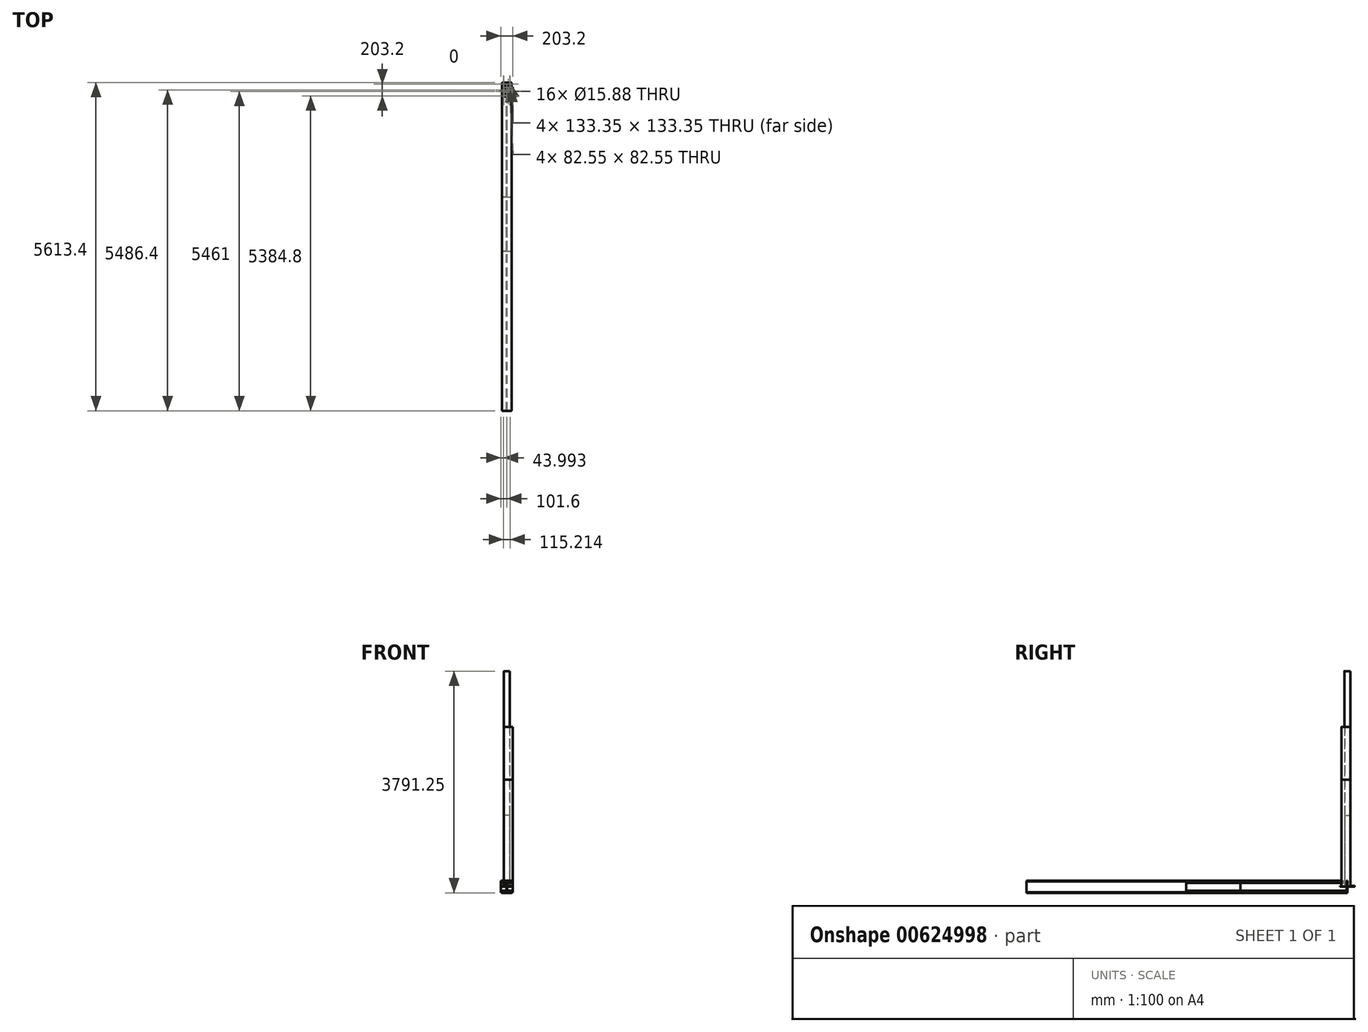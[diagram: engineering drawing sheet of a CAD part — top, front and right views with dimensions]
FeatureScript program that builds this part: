
annotation { "Feature Type Name" : "Feature", "Feature Type Description" : "" }
export const myFeature = defineFeature(function(context is Context, id is Id, definition is map)
    precondition{}
    {
        {
            assignVariable(context, id + "F0", {"name" : "length", "anyValue" : 5486.4 * mm});
        }
        {
            assignVariable(context, id + "F1", {"name" : "width", "anyValue" : 108});
        }
        {
            var Q0;
            Q0=qCreatedBy(makeId("Front.planeOp"),FACE);
            var sketch = newSketch(context, id + "F2", { "sketchPlane" : qUnion([Q0])});
            skLineSegment(sketch, "E0.bottom", {"start": v(83, -102.36) * mm, "end": v(-83, -102.36) * mm, "construction": true});
            skLineSegment(sketch, "E0.top", {"start": v(83, 102.36) * mm, "end": v(-83, 102.36) * mm, "construction": true});
            skLineSegment(sketch, "E0.left", {"start": v(83, -102.36) * mm, "end": v(83, 102.36) * mm, "construction": true});
            skLineSegment(sketch, "E0.right", {"start": v(-83, -102.36) * mm, "end": v(-83, 102.36) * mm, "construction": true});
            skPoint(sketch, "E0.middle", {"position": v(0, 0) * mm});
            skLineSegment(sketch, "E1", {"start": v(0, 102.36) * mm, "end": v(0, -102.36) * mm, "construction": true});
            skLineSegment(sketch, "E2", {"start": v(-83, 0) * mm, "end": v(83, 0) * mm, "construction": true});
            skLineSegment(sketch, "E3", {"start": v(-3.62, 0) * mm, "end": v(-3.62, 90.55) * mm});
            skLineSegment(sketch, "E4", {"start": v(-3.62, 90.55) * mm, "end": v(-83, 90.55) * mm});
            skLineSegment(sketch, "E5", {"start": v(-83, 90.55) * mm, "end": v(-83, 102.36) * mm});
            skLineSegment(sketch, "E6", {"start": v(-83, 102.36) * mm, "end": v(0, 102.36) * mm});
            skLineSegment(sketch, "E7.MirrorCS", {"start": v(83, 102.36) * mm, "end": v(0, 102.36) * mm});
            skLineSegment(sketch, "E8.MirrorCS", {"start": v(83, 90.55) * mm, "end": v(83, 102.36) * mm});
            skLineSegment(sketch, "E9.MirrorCS", {"start": v(3.62, 90.55) * mm, "end": v(83, 90.55) * mm});
            skLineSegment(sketch, "E10.MirrorCS", {"start": v(3.62, 0) * mm, "end": v(3.62, 90.55) * mm});
            skLineSegment(sketch, "E11.MirrorCS", {"start": v(-3.62, 0) * mm, "end": v(-3.62, -90.55) * mm});
            skLineSegment(sketch, "E12.MirrorCS", {"start": v(-3.62, -90.55) * mm, "end": v(-83, -90.55) * mm});
            skLineSegment(sketch, "E13.MirrorCS", {"start": v(-83, -90.55) * mm, "end": v(-83, -102.36) * mm});
            skLineSegment(sketch, "E14.MirrorCS", {"start": v(-83, -102.36) * mm, "end": v(0, -102.36) * mm});
            skLineSegment(sketch, "E15.MirrorCS", {"start": v(83, -102.36) * mm, "end": v(0, -102.36) * mm});
            skLineSegment(sketch, "E16.MirrorCS", {"start": v(83, -90.55) * mm, "end": v(83, -102.36) * mm});
            skLineSegment(sketch, "E17.MirrorCS", {"start": v(3.62, -90.55) * mm, "end": v(83, -90.55) * mm});
            skLineSegment(sketch, "E18.MirrorCS", {"start": v(3.62, 0) * mm, "end": v(3.62, -90.55) * mm});
            skSolve(sketch);
        }
        {
            var Q0;
            Q0 = qSketchRegion(id + "F2", true);
            extrude(context, id + "F3", {"entities" : qUnion([Q0]), "depth" : getVariable(context, 'length'), "offsetDistance" : 25.4 * mm});
        }
        {
            var Q0;
            Q0 = qSketchRegion(id + "F2", true);
            extrude(context, id + "F4", {"entities" : qUnion([Q0]), "depth" : (getVariable(context, 'width')) * mm, "offsetDistance" : 25.4 * mm});
        }
        {
            var Q0;
            Q0=qCreatedBy(makeId("Front.planeOp"),FACE);
            var sketch = newSketch(context, id + "F5", { "sketchPlane" : qUnion([Q0])});
            skLineSegment(sketch, "E19.bottom", {"start": v(77.22, -81.03) * mm, "end": v(-77.22, -81.03) * mm, "construction": true});
            skLineSegment(sketch, "E19.top", {"start": v(77.22, 81.03) * mm, "end": v(-77.22, 81.03) * mm, "construction": true});
            skLineSegment(sketch, "E19.left", {"start": v(77.22, -81.03) * mm, "end": v(77.22, 81.03) * mm, "construction": true});
            skLineSegment(sketch, "E19.right", {"start": v(-77.22, -81.03) * mm, "end": v(-77.22, 81.03) * mm, "construction": true});
            skPoint(sketch, "E19.middle", {"position": v(0, 0) * mm});
            skLineSegment(sketch, "E20", {"start": v(0, 81.03) * mm, "end": v(0, -81.03) * mm, "construction": true});
            skLineSegment(sketch, "E21", {"start": v(-77.22, 0) * mm, "end": v(77.22, 0) * mm, "construction": true});
            skLineSegment(sketch, "E22", {"start": v(-4.06, 0) * mm, "end": v(-4.06, 69.47) * mm});
            skLineSegment(sketch, "E23", {"start": v(-4.06, 69.47) * mm, "end": v(-77.22, 69.47) * mm});
            skLineSegment(sketch, "E24", {"start": v(-77.22, 69.47) * mm, "end": v(-77.22, 81.03) * mm});
            skLineSegment(sketch, "E25", {"start": v(-77.22, 81.03) * mm, "end": v(0, 81.03) * mm});
            skLineSegment(sketch, "E26.MirrorCS", {"start": v(77.22, 81.03) * mm, "end": v(0, 81.03) * mm});
            skLineSegment(sketch, "E27.MirrorCS", {"start": v(77.22, 69.47) * mm, "end": v(77.22, 81.03) * mm});
            skLineSegment(sketch, "E28.MirrorCS", {"start": v(4.06, 69.47) * mm, "end": v(77.22, 69.47) * mm});
            skLineSegment(sketch, "E29.MirrorCS", {"start": v(4.06, 0) * mm, "end": v(4.06, 69.47) * mm});
            skLineSegment(sketch, "E30.MirrorCS", {"start": v(-4.06, 0) * mm, "end": v(-4.06, -69.47) * mm});
            skLineSegment(sketch, "E31.MirrorCS", {"start": v(-4.06, -69.47) * mm, "end": v(-77.22, -69.47) * mm});
            skLineSegment(sketch, "E32.MirrorCS", {"start": v(-77.22, -69.47) * mm, "end": v(-77.22, -81.03) * mm});
            skLineSegment(sketch, "E33.MirrorCS", {"start": v(-77.22, -81.03) * mm, "end": v(0, -81.03) * mm});
            skLineSegment(sketch, "E34.MirrorCS", {"start": v(77.22, -81.03) * mm, "end": v(0, -81.03) * mm});
            skLineSegment(sketch, "E35.MirrorCS", {"start": v(77.22, -69.47) * mm, "end": v(77.22, -81.03) * mm});
            skLineSegment(sketch, "E36.MirrorCS", {"start": v(4.06, -69.47) * mm, "end": v(77.22, -69.47) * mm});
            skLineSegment(sketch, "E37.MirrorCS", {"start": v(4.06, 0) * mm, "end": v(4.06, -69.47) * mm});
            skSolve(sketch);
        }
        {
            var Q0;
            Q0 = qSketchRegion(id + "F5", true);
            extrude(context, id + "F6", {"entities" : qUnion([Q0]), "depth" : 2754.73 * mm, "offsetDistance" : 25.4 * mm});
        }
        {
            var Q0;
            Q0 = qSketchRegion(id + "F5", true);
            extrude(context, id + "F7", {"entities" : qUnion([Q0]), "depth" : 1828.8 * mm, "offsetDistance" : 25.4 * mm});
        }
        {
            var Q0;
            Q0=qCreatedBy(makeId("Top.planeOp"),FACE);
            var sketch = newSketch(context, id + "F8", { "sketchPlane" : qUnion([Q0])});
            skLineSegment(sketch, "E38.bottom", {"start": v(47.63, -50.8) * mm, "end": v(-47.63, -50.8) * mm});
            skLineSegment(sketch, "E38.top", {"start": v(47.63, 50.8) * mm, "end": v(-47.63, 50.8) * mm});
            skLineSegment(sketch, "E38.left", {"start": v(50.8, -47.62) * mm, "end": v(50.8, 47.63) * mm});
            skLineSegment(sketch, "E38.right", {"start": v(-50.8, -47.63) * mm, "end": v(-50.8, 47.63) * mm});
            skPoint(sketch, "E38.middle", {"position": v(0, 0) * mm});
            skLineSegment(sketch, "E39.bottom", {"start": v(41.28, -41.28) * mm, "end": v(-41.28, -41.28) * mm});
            skLineSegment(sketch, "E39.top", {"start": v(41.28, 41.28) * mm, "end": v(-41.28, 41.27) * mm});
            skLineSegment(sketch, "E39.left", {"start": v(41.28, -41.28) * mm, "end": v(41.28, 41.27) * mm});
            skLineSegment(sketch, "E39.right", {"start": v(-41.28, -41.28) * mm, "end": v(-41.28, 41.27) * mm});
            skPoint(sketch, "E40.visualSharp", {"position": v(-50.8, 50.8) * mm});
            skArc(sketch, "E40.filletArc", {"start": v(-47.63, 50.8) * mm, "mid": v(-49.87, 49.87) * mm, "end": v(-50.8, 47.63) * mm});
            skPoint(sketch, "E41.visualSharp", {"position": v(50.8, 50.8) * mm});
            skArc(sketch, "E41.filletArc", {"start": v(50.8, 47.63) * mm, "mid": v(49.87, 49.87) * mm, "end": v(47.63, 50.8) * mm});
            skPoint(sketch, "E42.visualSharp", {"position": v(50.8, -50.8) * mm});
            skArc(sketch, "E42.filletArc", {"start": v(47.63, -50.8) * mm, "mid": v(49.87, -49.87) * mm, "end": v(50.8, -47.62) * mm});
            skPoint(sketch, "E43.visualSharp", {"position": v(-50.8, -50.8) * mm});
            skArc(sketch, "E43.filletArc", {"start": v(-50.8, -47.63) * mm, "mid": v(-49.87, -49.87) * mm, "end": v(-47.63, -50.8) * mm});
            skSolve(sketch);
        }
        {
            var Q0;
            Q0 = qSketchRegion(id + "F8", true);
            extrude(context, id + "F9", {"entities" : qUnion([Q0]), "depth" : 1219.2 * mm, "offsetDistance" : 25.4 * mm});
        }
        {
            var Q0;
            Q0=qCreatedBy(makeId("Top.planeOp"),FACE);
            var sketch = newSketch(context, id + "F10", { "sketchPlane" : qUnion([Q0])});
            skLineSegment(sketch, "E44.bottom", {"start": v(98.42, -101.6) * mm, "end": v(-47.63, -101.6) * mm});
            skLineSegment(sketch, "E44.top", {"start": v(98.42, 50.8) * mm, "end": v(-47.63, 50.8) * mm});
            skLineSegment(sketch, "E44.left", {"start": v(101.6, -98.43) * mm, "end": v(101.6, 47.63) * mm});
            skLineSegment(sketch, "E44.right", {"start": v(-50.8, -98.43) * mm, "end": v(-50.8, 47.63) * mm});
            skPoint(sketch, "E44.middle", {"position": v(25.4, -25.4) * mm});
            skLineSegment(sketch, "E45.bottom", {"start": v(92.08, -92.08) * mm, "end": v(-41.28, -92.08) * mm});
            skLineSegment(sketch, "E45.top", {"start": v(92.08, 41.28) * mm, "end": v(-41.28, 41.27) * mm});
            skLineSegment(sketch, "E45.left", {"start": v(92.08, -92.08) * mm, "end": v(92.08, 41.28) * mm});
            skLineSegment(sketch, "E45.right", {"start": v(-41.28, -92.08) * mm, "end": v(-41.28, 41.28) * mm});
            skPoint(sketch, "E46.visualSharp", {"position": v(-50.8, 50.8) * mm});
            skArc(sketch, "E46.filletArc", {"start": v(-47.63, 50.8) * mm, "mid": v(-49.87, 49.87) * mm, "end": v(-50.8, 47.63) * mm});
            skPoint(sketch, "E47.visualSharp", {"position": v(101.6, 50.8) * mm});
            skArc(sketch, "E47.filletArc", {"start": v(101.6, 47.63) * mm, "mid": v(100.67, 49.87) * mm, "end": v(98.42, 50.8) * mm});
            skPoint(sketch, "E48.visualSharp", {"position": v(101.6, -101.6) * mm});
            skArc(sketch, "E48.filletArc", {"start": v(98.42, -101.6) * mm, "mid": v(100.67, -100.67) * mm, "end": v(101.6, -98.43) * mm});
            skPoint(sketch, "E49.visualSharp", {"position": v(-50.8, -101.6) * mm});
            skArc(sketch, "E49.filletArc", {"start": v(-50.8, -98.43) * mm, "mid": v(-49.87, -100.67) * mm, "end": v(-47.63, -101.6) * mm});
            skSolve(sketch);
        }
        {
            var Q0;
            Q0 = qSketchRegion(id + "F10", true);
            extrude(context, id + "F11", {"entities" : qUnion([Q0]), "depth" : 1828.8 * mm, "offsetDistance" : 25.4 * mm});
        }
        {
            var Q0;
            Q0 = qSketchRegion(id + "F8", true);
            extrude(context, id + "F12", {"entities" : qUnion([Q0]), "depth" : 3688.9 * mm, "offsetDistance" : 25.4 * mm});
        }
        {
            var Q0;
            Q0=qCreatedBy(makeId("Top.planeOp"),FACE);
            var sketch = newSketch(context, id + "F13", { "sketchPlane" : qUnion([Q0])});
            skLineSegment(sketch, "E50.bottom", {"start": v(83, -127) * mm, "end": v(-83, -127) * mm});
            skLineSegment(sketch, "E50.top", {"start": v(83, 127) * mm, "end": v(-83, 127) * mm});
            skLineSegment(sketch, "E50.left", {"start": v(83, -127) * mm, "end": v(83, 127) * mm});
            skLineSegment(sketch, "E50.right", {"start": v(-83, -127) * mm, "end": v(-83, 127) * mm});
            skPoint(sketch, "E50.middle", {"position": v(0, 0) * mm});
            skLineSegment(sketch, "E51", {"start": v(0, 127) * mm, "end": v(0, -127) * mm, "construction": true});
            skLineSegment(sketch, "E52", {"start": v(-83, 0) * mm, "end": v(83, 0) * mm, "construction": true});
            skPoint(sketch, "E52.startSnap0", {"position": v(-83, 0) * mm});
            skCircle(sketch, "E53", {"center": v(-57.6, 101.6) * mm, "radius": 7.94 * mm});
            skCircle(sketch, "E54.MirrorC", {"center": v(57.6, 101.6) * mm, "radius": 7.94 * mm});
            skCircle(sketch, "E55.MirrorC", {"center": v(-57.6, -101.6) * mm, "radius": 7.94 * mm});
            skCircle(sketch, "E56.MirrorC", {"center": v(57.6, -101.6) * mm, "radius": 7.94 * mm});
            skSolve(sketch);
        }
        {
            var Q0;
            Q0 = qSketchRegion(id + "F13", true);
            extrude(context, id + "F14", {"entities" : qUnion([Q0]), "depth" : 12.7 * mm, "offsetDistance" : 25.4 * mm});
        }
        {
            var Q0;
            Q0=qCreatedBy(makeId("Top.planeOp"),FACE);
            var sketch = newSketch(context, id + "F15", { "sketchPlane" : qUnion([Q0])});
            skLineSegment(sketch, "E57.bottom", {"start": v(76.2, -76.2) * mm, "end": v(-76.2, -76.2) * mm});
            skLineSegment(sketch, "E57.top", {"start": v(76.2, 76.2) * mm, "end": v(-76.2, 76.2) * mm});
            skLineSegment(sketch, "E57.left", {"start": v(76.2, -76.2) * mm, "end": v(76.2, 76.2) * mm});
            skLineSegment(sketch, "E57.right", {"start": v(-76.2, -76.2) * mm, "end": v(-76.2, 76.2) * mm});
            skPoint(sketch, "E57.middle", {"position": v(0, 0) * mm});
            skLineSegment(sketch, "E58", {"start": v(-76.2, 76.2) * mm, "end": v(0, 0) * mm, "construction": true});
            skCircle(sketch, "E59", {"center": v(-63.5, 63.5) * mm, "radius": 4.76 * mm});
            skLineSegment(sketch, "E60", {"start": v(0, 76.2) * mm, "end": v(0, -76.2) * mm, "construction": true});
            skLineSegment(sketch, "E61", {"start": v(-76.2, 0) * mm, "end": v(76.2, 0) * mm, "construction": true});
            skCircle(sketch, "E62.MirrorC", {"center": v(63.5, 63.5) * mm, "radius": 4.76 * mm});
            skCircle(sketch, "E63.MirrorC", {"center": v(-63.5, -63.5) * mm, "radius": 4.76 * mm});
            skCircle(sketch, "E64.MirrorC", {"center": v(63.5, -63.5) * mm, "radius": 4.76 * mm});
            skSolve(sketch);
        }
        {
            var Q0;
            Q0 = qSketchRegion(id + "F15", true);
            extrude(context, id + "F16", {"entities" : qUnion([Q0]), "depth" : 12.7 * mm, "offsetDistance" : 25.4 * mm});
        }
        {
            var Q0;
            Q0=qCreatedBy(makeId("Top.planeOp"),FACE);
            var sketch = newSketch(context, id + "F17", { "sketchPlane" : qUnion([Q0])});
            skLineSegment(sketch, "E65.bottom", {"start": v(77.22, -127) * mm, "end": v(-77.22, -127) * mm});
            skLineSegment(sketch, "E65.top", {"start": v(77.22, 127) * mm, "end": v(-77.22, 127) * mm});
            skLineSegment(sketch, "E65.left", {"start": v(77.22, -127) * mm, "end": v(77.22, 127) * mm});
            skLineSegment(sketch, "E65.right", {"start": v(-77.22, -127) * mm, "end": v(-77.22, 127) * mm});
            skPoint(sketch, "E65.middle", {"position": v(0, 0) * mm});
            skCircle(sketch, "E66", {"center": v(-51.82, 101.6) * mm, "radius": 7.94 * mm});
            skLineSegment(sketch, "E67", {"start": v(0, 127) * mm, "end": v(0, 0) * mm, "construction": true});
            skLineSegment(sketch, "E68", {"start": v(-77.22, 0) * mm, "end": v(77.22, 0) * mm, "construction": true});
            skCircle(sketch, "E69.MirrorC", {"center": v(51.82, 101.6) * mm, "radius": 7.94 * mm});
            skCircle(sketch, "E70.MirrorC", {"center": v(-51.82, -101.6) * mm, "radius": 7.94 * mm});
            skCircle(sketch, "E71.MirrorC", {"center": v(51.82, -101.6) * mm, "radius": 7.94 * mm});
            skSolve(sketch);
        }
        {
            var Q0;
            Q0 = qSketchRegion(id + "F17", true);
            extrude(context, id + "F18", {"entities" : qUnion([Q0]), "depth" : 12.7 * mm, "offsetDistance" : 25.4 * mm});
        }
        {
            var Q0;
            Q0=qCreatedBy(makeId("Front.planeOp"),FACE);
            var sketch = newSketch(context, id + "F19", { "sketchPlane" : qUnion([Q0])});
            skLineSegment(sketch, "E72.bottom", {"start": v(101.6, -101.6) * mm, "end": v(-101.6, -101.6) * mm});
            skLineSegment(sketch, "E72.top", {"start": v(101.6, 101.6) * mm, "end": v(-101.6, 101.6) * mm});
            skLineSegment(sketch, "E72.left", {"start": v(101.6, -101.6) * mm, "end": v(101.6, 101.6) * mm});
            skLineSegment(sketch, "E72.right", {"start": v(-101.6, -101.6) * mm, "end": v(-101.6, 101.6) * mm});
            skPoint(sketch, "E72.middle", {"position": v(0, 0) * mm});
            skCircle(sketch, "E73", {"center": v(-80.96, 80.96) * mm, "radius": 6.35 * mm});
            skLineSegment(sketch, "E74", {"start": v(-101.6, 101.6) * mm, "end": v(0, 0) * mm, "construction": true});
            skCircle(sketch, "E75.1.0", {"center": v(-80.96, -80.96) * mm, "radius": 6.35 * mm});
            skCircle(sketch, "E75.2.0", {"center": v(80.96, -80.96) * mm, "radius": 6.35 * mm});
            skCircle(sketch, "E75.3.0", {"center": v(80.96, 80.96) * mm, "radius": 6.35 * mm});
            skLineSegment(sketch, "E76", {"start": v(0, 0) * mm, "end": v(0, 101.6) * mm, "construction": true});
            skSolve(sketch);
        }
        {
            var Q0;
            Q0 = qSketchRegion(id + "F19", true);
            extrude(context, id + "F20", {"entities" : qUnion([Q0]), "depth" : 12.7 * mm, "offsetDistance" : 25.4 * mm});
        }
        {
            var Q0;
            Q0 = qSketchRegion(id + "F10", true);
            extrude(context, id + "F21", {"entities" : qUnion([Q0]), "depth" : 2731.36 * mm, "offsetDistance" : 25.4 * mm});
        }
    });
